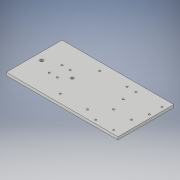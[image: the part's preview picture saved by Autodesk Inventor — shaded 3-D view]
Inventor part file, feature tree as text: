
AUTODESK INVENTOR PART (.ipt)
format: ipt  version: 2017 (Build 210142000, 142)  size: 145,408 bytes
history: native  units: in
note: dims shown in document units (in); Inventor stores cm internally (conversion verified against a paired STEP export)
features: extrude x1, sketch x1
ambient origin geometry x8: Origin, YZ Plane, XZ Plane, XY Plane, X Axis, Y Axis, Z Axis, Center Point
bodies: Solid1 (feature_tree)
feature tree (2):
  extrude  "Extrusion1"  Depth=5.0in
  sketch  "Sketch1"  dims[d0=10.0in d1=5.0in d2=0.15in d3=0.15in d4=0.15in d5=0.15in d6=1.6in d7=1.6in d8=1.6in d9=1.6in d14=0.15in d15=0.15in d16=0.15in d17=0.15in d18=0.3in d19=2.5in d20=0.25in d21=2.74in d22=2.5in d25=0.15in d26=0.15in d27=0.15in d28=0.15in d31=0.15in d32=0.15in d33=0.15in d34=0.15in d35=0.25in d36=0.0in]
